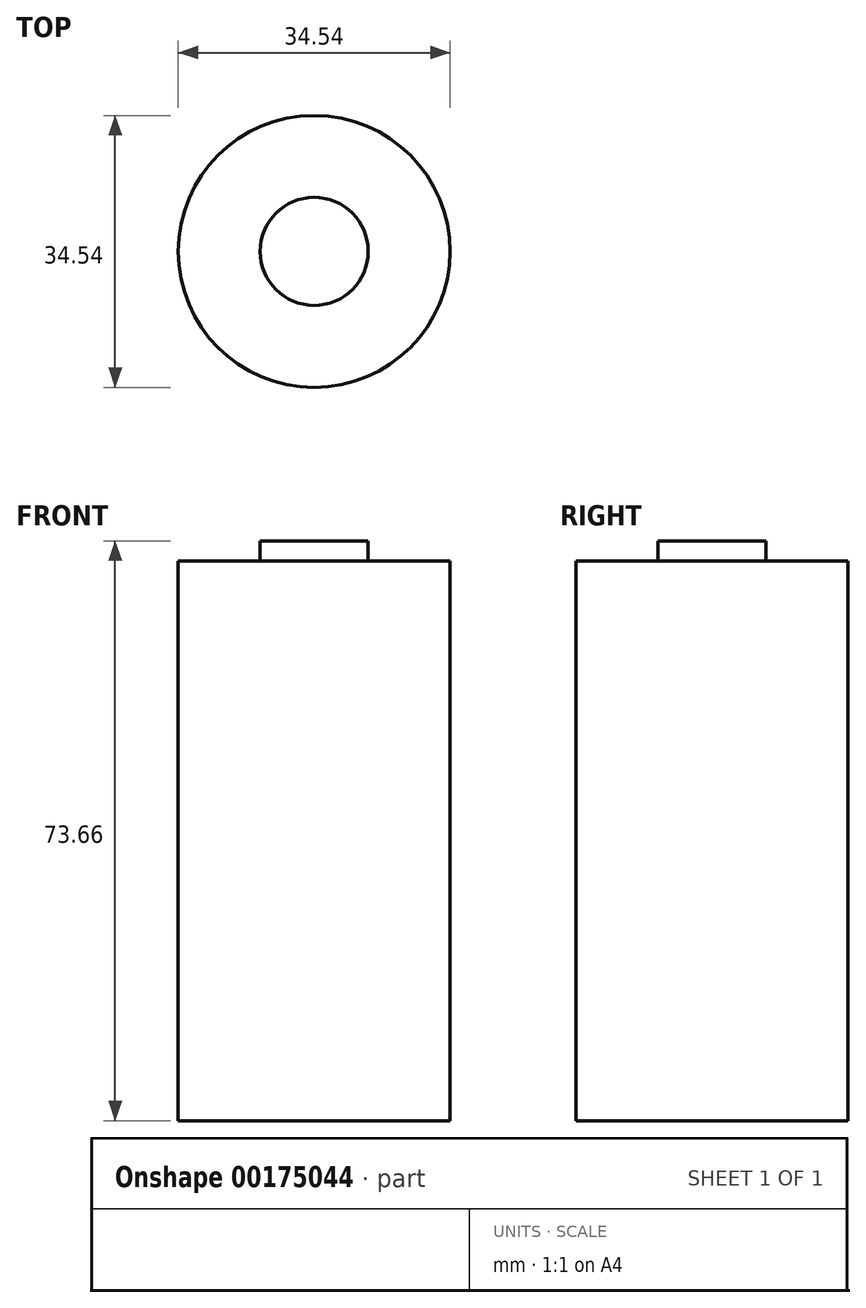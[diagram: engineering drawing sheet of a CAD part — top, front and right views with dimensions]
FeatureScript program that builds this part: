
annotation { "Feature Type Name" : "Feature", "Feature Type Description" : "" }
export const myFeature = defineFeature(function(context is Context, id is Id, definition is map)
    precondition{}
    {
        {
            var Q0;
            Q0=qCreatedBy(makeId("Front.planeOp"),FACE);
            var sketch = newSketch(context, id + "F0", { "sketchPlane" : qUnion([Q0])});
            skLineSegment(sketch, "E0", {"start": v(0, 44.7) * mm, "end": v(0, -42.42) * mm});
            skLineSegment(sketch, "E1", {"start": v(-17.27, 36.58) * mm, "end": v(-17.27, -34.54) * mm});
            skLineSegment(sketch, "E2", {"start": v(-17.27, 36.58) * mm, "end": v(0, 36.58) * mm});
            skLineSegment(sketch, "E3", {"start": v(-17.27, -34.54) * mm, "end": v(0, -34.54) * mm});
            skSolve(sketch);
        }
        {
            var Q0;
            Q0 = qSketchRegion(id + "F0", true);
            var Q1;
            Q1=sQuery(id+"F0.wireOp",EDGE,"E0");
            revolve(context, id + "F1", {"entities" : qUnion([Q0]), "axis" : qUnion([Q1]), "revolveType" : RevolveType.FULL});
        }
        {
            var Q0;
            Q0=makeQuery(id+"F1.opRevolve","SWEPT_FACE",FACE,{"disambiguationData":[OSD([sQuery(id+"F0.wireOp",EDGE,"E2")])]});
            var sketch = newSketch(context, id + "F2", { "sketchPlane" : qUnion([Q0])});
            skCircle(sketch, "E4", {"center": v(0, 0) * mm, "radius": 6.86 * mm});
            skSolve(sketch);
        }
        {
            var Q0;
            Q0 = qSketchRegion(id + "F2", true);
            extrude(context, id + "F3", {"entities" : qUnion([Q0]), "operationType" : NewBodyOperationType.ADD, "depth" : 2.54 * mm, "offsetDistance" : 25.4 * mm});
        }
    });
